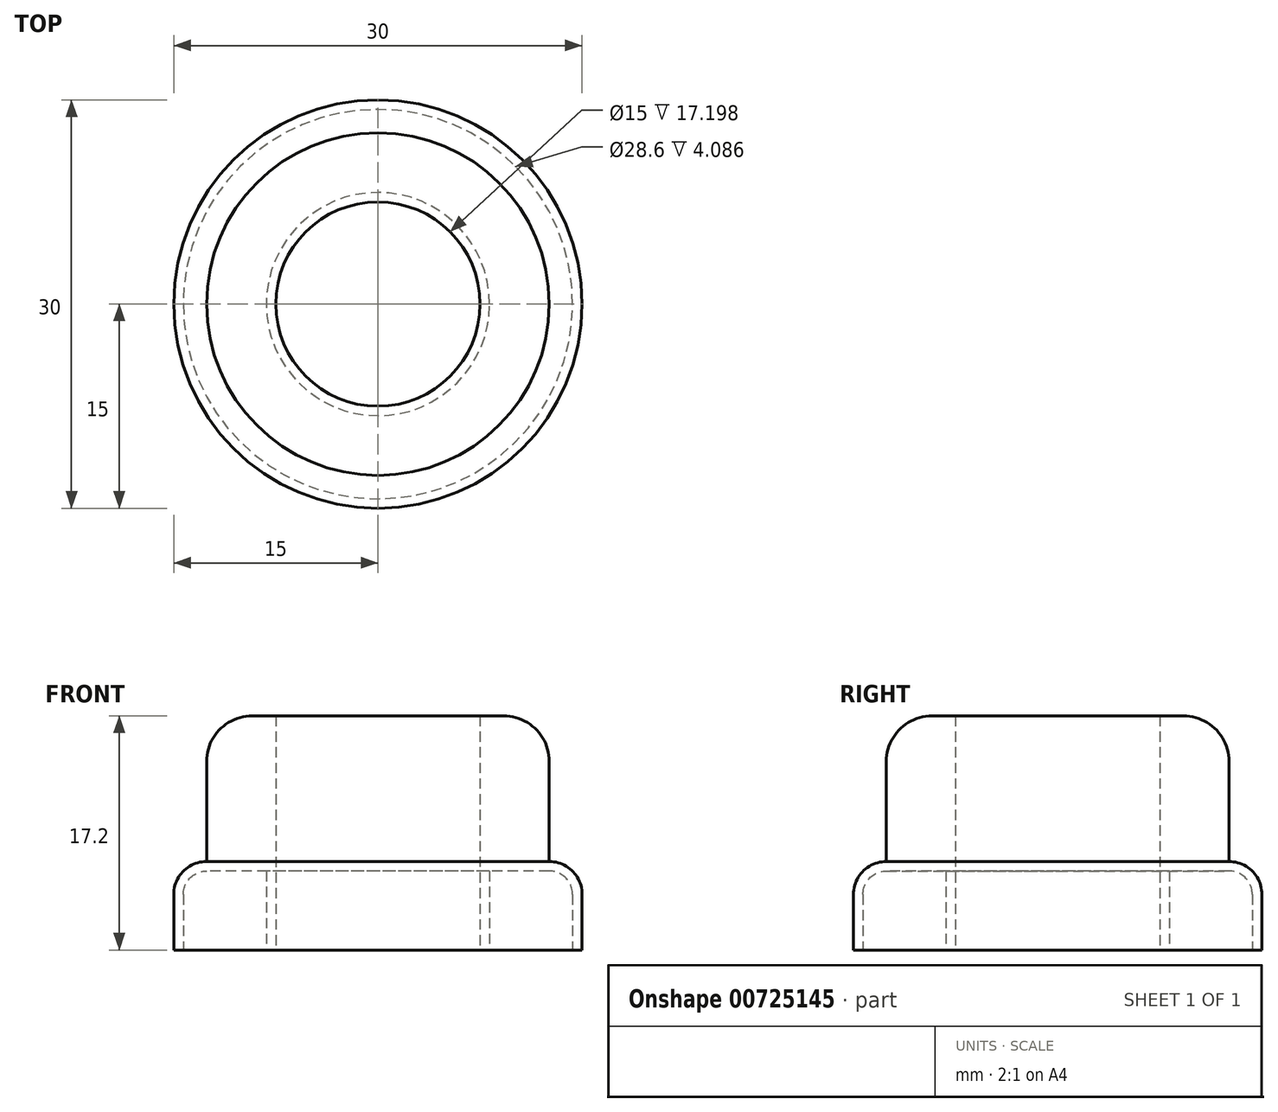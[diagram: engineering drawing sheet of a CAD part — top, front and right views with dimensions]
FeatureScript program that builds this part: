
annotation { "Feature Type Name" : "Feature", "Feature Type Description" : "" }
export const myFeature = defineFeature(function(context is Context, id is Id, definition is map)
    precondition{}
    {
        {
            var Q0;
            Q0=qCreatedBy(makeId("Top.planeOp"),FACE);
            var sketch = newSketch(context, id + "F0", { "sketchPlane" : qUnion([Q0])});
            skCircle(sketch, "E0", {"center": v(0, 0) * mm, "radius": 15 * mm});
            skSolve(sketch);
        }
        {
            var Q0;
            Q0=makeQuery(id+"F0.imprint","IMPRINT",FACE,{"disambiguationData":[TD([[makeQuery(id+"F0.imprint","IMPRINT",EDGE,{"derivedFrom":sQuery(id+"F0.wireOp",EDGE,"E0")}),1.0]])]});
            extrude(context, id + "F1", {"entities" : qUnion([Q0]), "depth" : 6.5 * mm, "offsetDistance" : 25 * mm});
        }
        {
            var Q0;
            Q0=makeQuery(id+"F1.opExtrude","CAP_FACE",FACE,{"disambiguationData":[OSD([sQuery(id+"F0.wireOp",EDGE,"E0")])],"isStart":false});
            fillet(context, id + "F2", {"entities" : qUnion([Q0]), "radius" : 2.41 * mm, "tangentPropagation" : true, "allowEdgeOverflow" : false});
        }
        {
            var Q0;
            Q0=qCreatedBy(makeId("Top.planeOp"),FACE);
            var sketch = newSketch(context, id + "F3", { "sketchPlane" : qUnion([Q0])});
            skCircle(sketch, "E1", {"center": v(0, 0) * mm, "radius": 5.9 * mm});
            skSolve(sketch);
        }
        {
            var Q0;
            Q0=sQuery(id+"F3.wireOp",VERTEX,"E1.center");
            var Q1;
            Q1=makeQuery(id+"F1.opExtrude","SWEPT_BODY",BODY,{"disambiguationData":[OSD([sQuery(id+"F0.wireOp",EDGE,"E0")])]});
            hole(context, id + "F4", {"style" : HoleStyle.SIMPLE, "endStyle" : HoleEndStyle.THROUGH, "oppositeDirection" : true, "holeDiameter" : 15 * mm, "majorDiameter" : 5 * mm, "isTappedThrough" : true, "tappedDepth" : 12 * mm, "tapClearance" : 3, "locations" : qUnion([Q0]), "scope" : qUnion([Q1])});
        }
        {
            var Q0;
            Q0=makeQuery(id+"F1.opExtrude","CAP_FACE",FACE,{"disambiguationData":[OSD([sQuery(id+"F0.wireOp",EDGE,"E0")])],"isStart":true});
            shell(context, id + "F5", {"entities" : qUnion([Q0]), "thickness" : 0.7 * mm});
        }
        {
            var Q0;
            {var subQ0=sQuery(id+"F0.wireOp",EDGE,"E0");Q0=makeQuery(id+"F5.opShell","OFFSET_FACE",FACE,{"disambiguationData":[OSD([subQ0]),TDD([makeQuery(id+"F1.opExtrude","CAP_FACE",FACE,{"disambiguationData":[OSD([subQ0])],"isStart":false})])]});}
            var sketch = newSketch(context, id + "F6", { "sketchPlane" : qUnion([Q0])});
            skSolve(sketch);
        }
        {
            var Q0;
            Q0=makeQuery(id+"F1.opExtrude","CAP_FACE",FACE,{"disambiguationData":[OSD([sQuery(id+"F0.wireOp",EDGE,"E0")])],"isStart":false});
            extrude(context, id + "F7", {"entities" : qUnion([Q0]), "operationType" : NewBodyOperationType.ADD, "depth" : 10.7 * mm, "offsetDistance" : 25 * mm});
        }
        {
            var Q0;
            Q0=makeQuery(id+"F7.opExtrude","CAP_EDGE",EDGE,{"disambiguationData":[OSD([sQuery(id+"F0.wireOp",EDGE,"E0")])],"isStart":false});
            fillet(context, id + "F8", {"entities" : qUnion([Q0]), "radius" : 3.35 * mm, "tangentPropagation" : true, "allowEdgeOverflow" : false});
        }
    });
